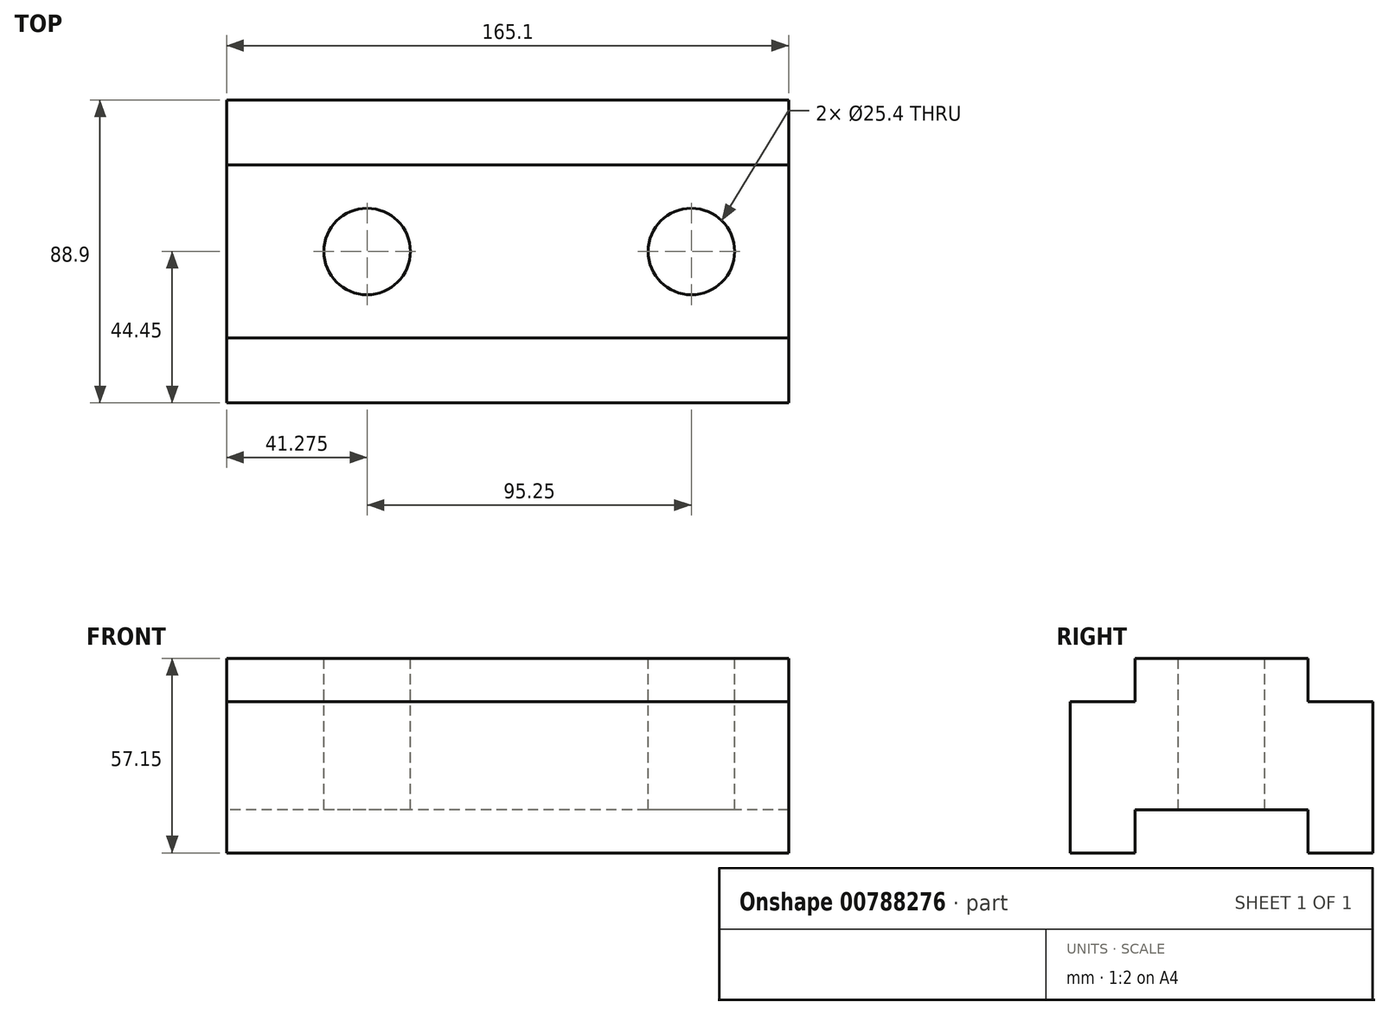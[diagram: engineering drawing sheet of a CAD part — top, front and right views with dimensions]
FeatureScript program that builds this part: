
annotation { "Feature Type Name" : "Feature", "Feature Type Description" : "" }
export const myFeature = defineFeature(function(context is Context, id is Id, definition is map)
    precondition{}
    {
        {
            var Q0;
            Q0=qCreatedBy(makeId("Right.planeOp"),FACE);
            var sketch = newSketch(context, id + "F0", { "sketchPlane" : qUnion([Q0])});
            skLineSegment(sketch, "E0", {"start": v(0, 0) * mm, "end": v(50.8, 0) * mm});
            skLineSegment(sketch, "E1", {"start": v(0, 0) * mm, "end": v(0, -12.7) * mm});
            skLineSegment(sketch, "E2", {"start": v(0, -12.7) * mm, "end": v(-19.05, -12.7) * mm});
            skLineSegment(sketch, "E3", {"start": v(50.8, 0) * mm, "end": v(50.8, -12.7) * mm});
            skLineSegment(sketch, "E4", {"start": v(50.8, -12.7) * mm, "end": v(69.85, -12.7) * mm});
            skLineSegment(sketch, "E5", {"start": v(-19.05, -12.7) * mm, "end": v(-19.05, 31.75) * mm});
            skLineSegment(sketch, "E6", {"start": v(69.85, -12.7) * mm, "end": v(69.85, 31.75) * mm});
            skLineSegment(sketch, "E7", {"start": v(69.85, 31.75) * mm, "end": v(50.8, 31.75) * mm});
            skLineSegment(sketch, "E8", {"start": v(-19.05, 31.75) * mm, "end": v(0, 31.75) * mm});
            skLineSegment(sketch, "E9", {"start": v(0, 31.75) * mm, "end": v(0, 44.45) * mm});
            skLineSegment(sketch, "E10", {"start": v(50.8, 31.75) * mm, "end": v(50.8, 44.45) * mm});
            skLineSegment(sketch, "E11", {"start": v(0, 44.45) * mm, "end": v(50.8, 44.45) * mm});
            skSolve(sketch);
        }
        {
            var Q0;
            Q0 = qSketchRegion(id + "F0", true);
            extrude(context, id + "F1", {"entities" : qUnion([Q0]), "depth" : 165.1 * mm, "offsetDistance" : 25.4 * mm});
        }
        {
            var Q0;
            Q0=makeQuery(id+"F1.opExtrude","SWEPT_FACE",FACE,{"disambiguationData":[OSD([sQuery(id+"F0.wireOp",EDGE,"E11")])]});
            var sketch = newSketch(context, id + "F2", { "sketchPlane" : qUnion([Q0])});
            skLineSegment(sketch, "E12", {"start": v(0, 25.4) * mm, "end": v(41.28, 25.4) * mm, "construction": true});
            skLineSegment(sketch, "E13", {"start": v(41.28, 25.4) * mm, "end": v(136.53, 25.4) * mm, "construction": true});
            skCircle(sketch, "E14", {"center": v(41.28, 25.4) * mm, "radius": 12.7 * mm});
            skCircle(sketch, "E15", {"center": v(136.53, 25.4) * mm, "radius": 12.7 * mm});
            skSolve(sketch);
        }
        {
            var Q0;
            Q0 = qSketchRegion(id + "F2", true);
            extrude(context, id + "F3", {"entities" : qUnion([Q0]), "operationType" : NewBodyOperationType.REMOVE, "endBound" : BoundingType.UP_TO_NEXT, "oppositeDirection" : true, "depth" : 25.4 * mm, "offsetDistance" : 25.4 * mm});
        }
    });
